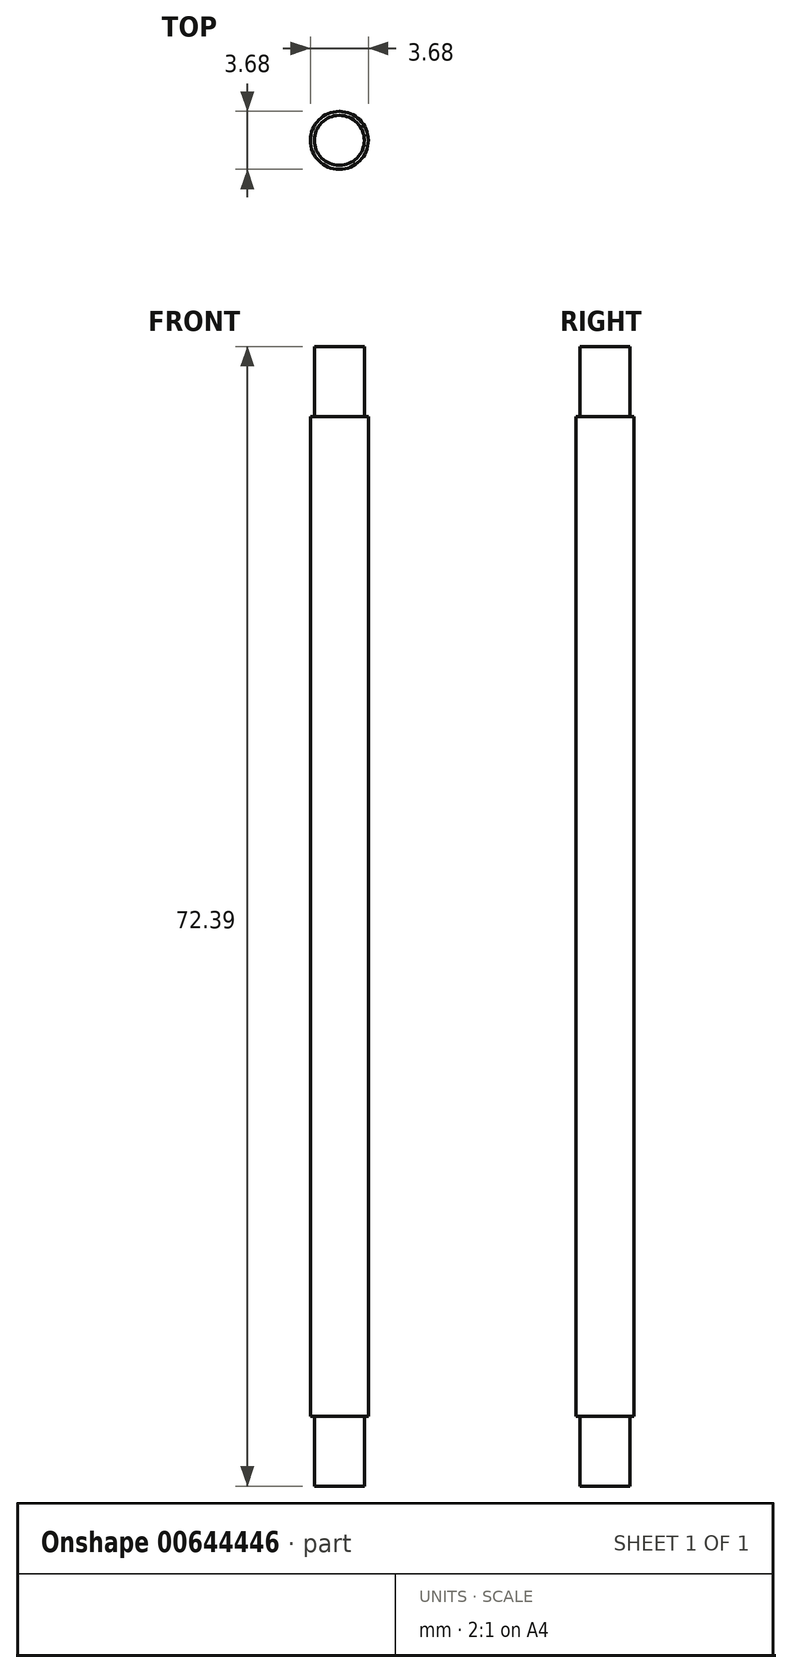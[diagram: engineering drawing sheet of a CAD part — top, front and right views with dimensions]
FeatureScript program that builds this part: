
annotation { "Feature Type Name" : "Feature", "Feature Type Description" : "" }
export const myFeature = defineFeature(function(context is Context, id is Id, definition is map)
    precondition{}
    {
        {
            var Q0;
            Q0=qCreatedBy(makeId("Front.planeOp"),FACE);
            var sketch = newSketch(context, id + "F0", { "sketchPlane" : qUnion([Q0])});
            skLineSegment(sketch, "E0", {"start": v(0, 0) * mm, "end": v(-1.59, 0) * mm});
            skLineSegment(sketch, "E1", {"start": v(-1.59, 0) * mm, "end": v(-1.59, 4.45) * mm});
            skLineSegment(sketch, "E2", {"start": v(-1.59, 4.45) * mm, "end": v(-1.84, 4.45) * mm});
            skLineSegment(sketch, "E3", {"start": v(-1.84, 4.45) * mm, "end": v(-1.84, 67.95) * mm});
            skLineSegment(sketch, "E4", {"start": v(-1.84, 67.95) * mm, "end": v(-1.59, 67.95) * mm});
            skLineSegment(sketch, "E5", {"start": v(-1.59, 67.95) * mm, "end": v(-1.59, 72.4) * mm});
            skLineSegment(sketch, "E6", {"start": v(-1.59, 72.4) * mm, "end": v(0, 72.4) * mm});
            skLineSegment(sketch, "E7", {"start": v(0, 72.4) * mm, "end": v(0, 0) * mm});
            skSolve(sketch);
        }
        {
            var Q0;
            Q0=makeQuery(id+"F0.imprint","IMPRINT",FACE,{"disambiguationData":[TD([[makeQuery(id+"F0.imprint","IMPRINT",EDGE,{"derivedFrom":sQuery(id+"F0.wireOp",EDGE,"E0")}),-1.0]])]});
            var Q1;
            Q1=sQuery(id+"F0.wireOp",EDGE,"E7");
            revolve(context, id + "F1", {"entities" : qUnion([Q0]), "axis" : qUnion([Q1]), "revolveType" : RevolveType.FULL});
        }
    });
